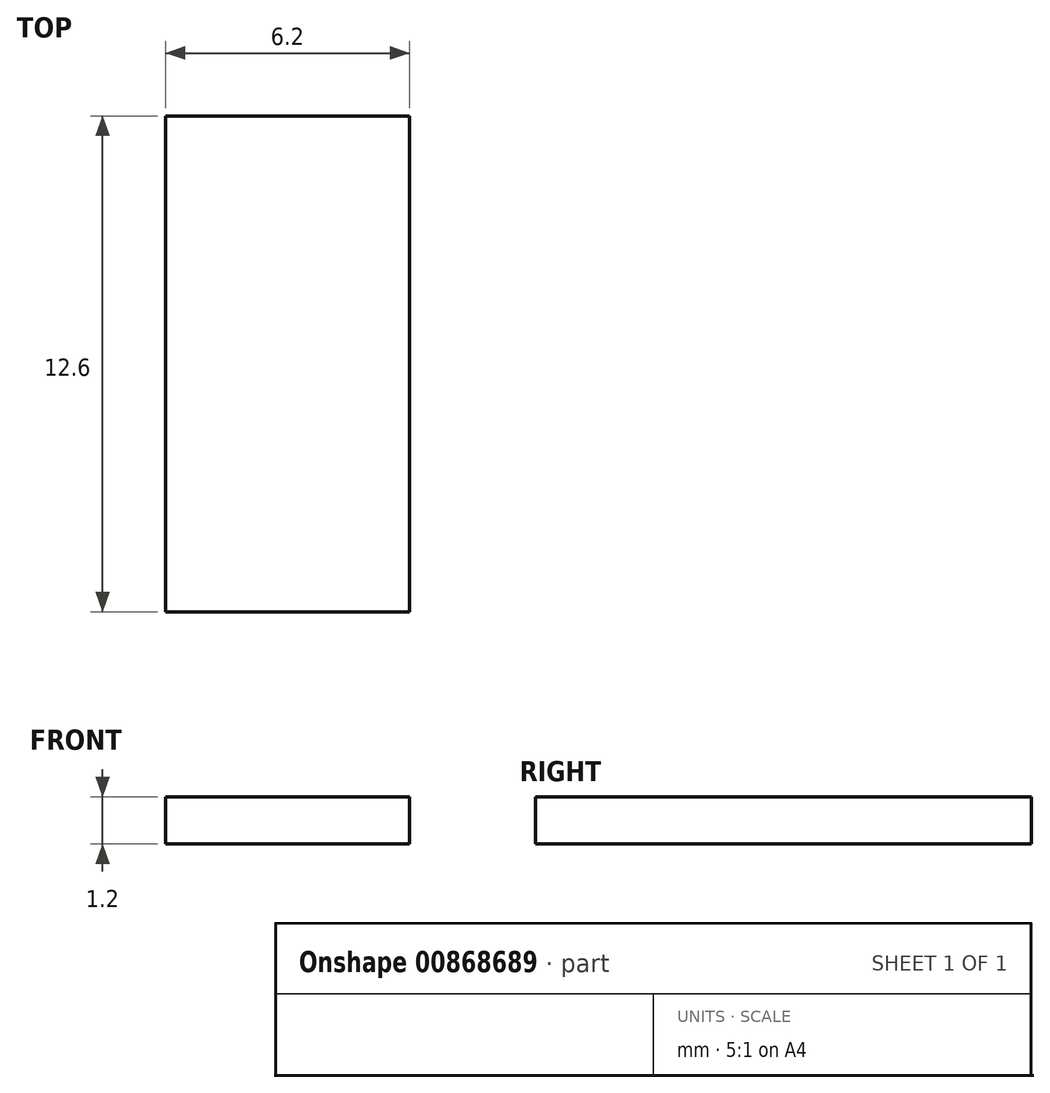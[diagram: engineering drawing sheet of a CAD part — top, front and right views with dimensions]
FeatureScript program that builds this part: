
annotation { "Feature Type Name" : "Feature", "Feature Type Description" : "" }
export const myFeature = defineFeature(function(context is Context, id is Id, definition is map)
    precondition{}
    {
        {
            var Q0;
            Q0=qCreatedBy(makeId("Top.planeOp"),FACE);
            var sketch = newSketch(context, id + "F0", { "sketchPlane" : qUnion([Q0])});
            skLineSegment(sketch, "E0.bottom", {"start": v(-3.1, 6.3) * mm, "end": v(3.1, 6.3) * mm});
            skLineSegment(sketch, "E0.top", {"start": v(-3.1, -6.3) * mm, "end": v(3.1, -6.3) * mm});
            skLineSegment(sketch, "E0.left", {"start": v(-3.1, 6.3) * mm, "end": v(-3.1, -6.3) * mm});
            skLineSegment(sketch, "E0.right", {"start": v(3.1, 6.3) * mm, "end": v(3.1, -6.3) * mm});
            skPoint(sketch, "E0.middle", {"position": v(0, 0) * mm});
            skSolve(sketch);
        }
        {
            var Q0;
            Q0=makeQuery(id+"F0.imprint","IMPRINT",FACE,{"disambiguationData":[TD([[makeQuery(id+"F0.imprint","IMPRINT",EDGE,{"derivedFrom":sQuery(id+"F0.wireOp",EDGE,"E0.bottom")}),-1.0]])]});
            extrude(context, id + "F1", {"entities" : qUnion([Q0]), "depth" : 1.2 * mm, "offsetDistance" : 25.4 * mm});
        }
    });
